# Revit family: PRD_AR_ShwrFttngsPckg_MIRANITShowerPanel_F5LT2024-F5LT2029
name_source: partatom
category: Plumbing Fixtures
units: mm (PartAtom-declared; Revit-internal decimal feet)

## family parameters
Cut with Voids When Loaded = No
Host = Face
OmniClass Number = 23.45.05.14.17
OmniClass Title = Showers
Part Type = Normal
Room Calculation Point = No
Round Connector Dimension = Use Diameter
Shared = No

## types (6) — shared parameters
AccentColour = chrome-look (glossy)
AdditionalConnections = no
AdjustableFlowTime = no
AssetType = Fixed
BasicColour = white
BodyMaterial = PRD_AR_MineralMaterial_Alpinewhite
Category = Pr_40_20_87_75, Shower fittings package
Circulation = no
Color = white
CompatibleA3000Open = no
ConnectionWithPayWaterDispenser = not possible
Default Elevation = 1500 mm  [stored 4.92126 ft]
DiameterNominal = 15  [stored 0.0492126 ft]
DurationUnit = year
FittingMaterial = PRD_AR_ChromatedBrass_HighPolished
FunctionalPrinciple = manual
IfcExportAs = IfcSanitaryTerminalType
IfcExportType = SHOWER
InletSize = G 1/2 A
LockingMechanism = Top section, ceramic
Manufacturer = KWC Group AG
ManufacturerName = KWC Group AG
ManufacturerURL = www.kwc.com
Material = mineral
MaterialCasing = mineral material
MaterialCodeCasing = Miranit
MaterialFitting = brass-look
MinimumFlowPressure = 1 bar
NBSDescription = Shower fittings package
NBSReference = 45-35-70/330
NominalDepth = 100 mm  [stored 0.328084 ft]
NominalHeight = 1160 mm  [stored 3.80577 ft]
NominalLength = 1160 mm  [stored 3.80577 ft]
NominalWidth = 235 mm  [stored 0.770997 ft]
OverallDepth = 100 mm
OverallHeight = 1160 mm
OverallWidth = 235 mm
PositionOfWaterConnection = from top / backside
ProductInformation = http://pim.kwc.com
ProtectiveShutdown = no
ShowerPipeDraining = no
ShowerType = Individual
Size = 235 x 1160 x 100 mm (W x H x D)
SoundInsulation = no
Status = New
SurfaceFinishFitting = chromed
SurfaceTreatmentFitting = polished
TailorMade = no
TemperatureLimit = yes
ThermalDisinfection = yes
TypeOfMixing = with thermostat
TypeOfMounting = wall mounting
TypeOfOperation = manual operation
TypeOfShower = shower panel
URL = www.kwc.com
Uniclass2015Code = Pr_40_20_87_75
Uniclass2015Title = Shower fittings package
Uniclass2015Version = Products v1.32
Version = 1
VolumeFlowRate = 0.15 l/s at 3 bar
WarrantyDurationUnit = year
WaterConnection = hose (gland nut)
WithBackflowPreventer = yes
WithFilter = yes
WithRosettesOrCoverPlate = yes
zero-valued in all types: DrainSize

## per-type parameters (varying)
| type | BIMObjectName | DefaultAutomaticHygieneFlush | Description | Features | ForHandShower | HandShowerVisibility | HasTray | HygieneFlushing | ModelNumber | Name | Parameterization | PositionOfPowerConnection | PowerSupplyConnection | ShowerGelShelf | ShowerHead | ShowerHeadVisibility | TypeOfPowerSupply | TypeOfSensor | WithShowerSet | WithSoapDish | WithTransformerOrPowerSupply |
| F5LT2024 | PRD_AR_ShowerFittingsPackage_MIRANITShowerPanel_F5LT2024 | fixed interval 24 hours | F5L-Therm shower panel made from mineral material for wall mounting with single-lever thermostat DN 15 and connecting nozzle for shower head. For connection to hot and cold water. Function block with integrated mixing cartridge and pre-assembled hygiene unit including sensor with control electronics to perform automatic water hygiene flushing, program-controlled thermal disinfection (additional bypass solenoid-operated flush valve cartridge necessary) and storage of statistical data. Thermostatically-controlled mixer cartridge with expansion element and active scald protection as well as adjustable and turn-proof temperature stop, and ceramic disc technology. All-metal construction, visible parts high-polished, chrome-plated. Connecting nozzles for separate required DN 15 KWC shower head with pre-fitted flow regulator 9.0l/min. Housing with raised function surface made of MIRANIT resin-bonded mineral material with pore-free smooth surface (temperature-resistant up to 80 °C), Alpine white colour. With adjustable and lockable connections with backflow preventer and strainers. Activated hygiene flushing, fixed interval of 24 hours. With option for parameterization and communication via optional, bidirectional remote control. Optional hygiene unit for battery operation with 6 V lithium battery (CR-P2) per fitting or separate power supply via plug-in power supply unit 6.75 V/12 V DC. | For connection to hot and cold water. Housing dimensions 235 x 1160 x 100 mm (W x H x D). Shower head and battery compartment including battery or powersupply unit with extension cable must be ordered separately. | no | No | No | yes | 2030066543 | F5L-Therm MIRANIT shower panel F5LT2024 | remote control | from top / backside | 6.75 / 12 V DC | No | for separately shower head | Yes | Other | opto-electronic sensor | no | no | no |
| F5LT2025 | PRD_AR_ShowerFittingsPackage_MIRANITShowerPanel_F5LT2025 | fixed interval 24 hours | F5L-Therm shower panel made from mineral material for wall mounting with single-lever thermostat DN 15 and hand shower fitting kit. For connection to hot and cold water. Function block with integrated mixing cartridge and pre-assembled hygiene unit including sensor with control electronics to perform automatic water hygiene flushing, program-controlled thermal disinfection (additional bypass solenoid-operated flush valve cartridge necessary) and storage of statistical data. Thermostatically-controlled mixer cartridge with expansion element and active scaldprotection as well as adjustable and turn-proof temperature stop, and ceramic disc technology. All-metal construction, visible parts high-polished, chrome-plated. Pre-fitted chrome-plated brass shower rail with height-adjustable hand shower holder and chrome-plated plastic hand shower, shower head with rain jet, diameter 110 mm, shower hose 900 mm. Housing with raised function surface made of MIRANIT resin-bonded mineral material with pore-free smooth surface (temperature-resistant up to 80 °C), Alpinewhite colour. With adjustable and lockable connections with backflow preventer and strainers. Activated hygiene flushing, fixed interval of 24 hours. With option for parameterization and communication via optional, bidirectional remote control. Optional hygiene unit for battery operation with 6 V lithium battery (CR-P2) per fitting or separate power supply via plug-in power supply unit 6.75 V/12 V DC. | For connection to hot and cold water. Housing dimensions 235 x 1160 x 100 mm (W x H x D). Battery compartment including battery or power supply unit with extension cable must be ordered separately. | yes | Yes | No | yes | 2030066544 | F5L-Therm MIRANIT shower panel with hand shower fitting kit F5LT2025 | remote control |  | 6.75 / 12 V DC | No |  | No | Other | opto-electronic sensor | yes | no | no |
| F5LT2026 | PRD_AR_ShowerFittingsPackage_MIRANITShowerPanel_F5LT2026 | fixed interval 24 hours | F5L-Therm shower panel made from mineral material for wall mounting with single-lever thermostat DN 15 and connecting nozzle for shower head. For connection to hot and cold water. Function block with integrated mixing cartridge and pre-assembled hygiene unit including sensor with control electronics to perform automatic water hygiene flushing, program-controlled thermal disinfection (additional bypass solenoid-operated flush valve cartridge necessary) and storage of statistical data. Thermostatically-controlled mixer cartridge with expansion element and active scald protection as well as adjustable and turn-proof temperature stop, and ceramic disc technology. All-metal construction, visible parts high-polished, chrome-plated. Connecting nozzles for separate required DN 15 KWC shower head with pre-fitted flow regulator 9.0l/min. Housing with raised function surface and seamless moulded shower gel shelf made of MIRANIT resin-bonded mineral material with pore-free smooth surface (temperature-resistant up to 80 °C), Alpine white colour. With adjustable and lockable connections with backflow preventer and strainers. Activated hygiene flushing, fixed interval of 24 hours. With option for parameterization and communication via optional, bidirectional remote control. Optional hygiene unit for battery operation with 6 V lithium battery (CR-P2) per fitting or separate power supply via plug-in power supply unit 6.75 V/12 V DC. | For connection to hot and cold water. Housing dimensions 235 x 1160 x 100 mm (W x H x D). Shower head and battery compartment including battery or power supply unit with extension cable must be ordered separately. | no | No | Yes | yes | 2030066546 | F5L-Therm MIRANIT shower panel with shower gel shelf F5LT2026 | remote control | from top / backside | 6.75 / 12 V DC | Yes | for separately shower head | Yes | Other | opto-electronic sensor | no | integrated | no |
| F5LT2027 | PRD_AR_ShowerFittingsPackage_MIRANITShowerPanel_F5LT2027 |  | F5L-Therm shower panel made from mineral material for wall mounting with single-lever thermostat DN 15 and connecting nozzle for shower head. For connection to hot and cold water. Function block with integrated mixing cartridge and mechanism for an optional water hygiene unit for automatic water hygiene flushing, program-controlled thermal disinfection (additional bypass solenoid-operated flush valve cartridge necessary) and storage of statistical data. Thermostatically-controlled mixer cartridge with expansion element and active scald protection as well as adjustable and turn-proof temperature stop, and ceramic disc technology. All-metal construction, visible parts high-polished, chrome-plated. Connecting nozzles for separate required DN 15 KWC shower head with pre-fitted flow regulator 9.0 l/min. Housing with raised function surface made of MIRANIT resin-bonded mineral material with pore-free smooth surface (temperature-resistant up to 80 °C), Alpine white colour. With adjustable and lockable connections with backflow preventer and strainers. | For connection to hot and cold water. Housing dimensions 235 x 1160 x 100 mm (W x H x D). Shower head must be ordered separately. | no | No | No | prepared | 2030066547 | F5L-Therm MIRANIT shower panel F5LT2027 |  |  |  | No | for separately shower head | Yes |  |  | no | no |  |
| F5LT2028 | PRD_AR_ShowerFittingsPackage_MIRANITShowerPanel_F5LT2028 |  | F5L-Therm shower panel made from mineral material for wall mounting with single-lever thermostat DN 15 and hand shower fitting kit. For connection to hot and cold water. Function block with integrated mixing cartridge and mechanism for an optional water hygiene unit for automatic water hygiene flushing, program-controlled thermal disinfection (additional bypass solenoid-operated flush valve cartridge necessary) and storage of statistical data. Thermostatically-controlled mixer cartridge with expansion element and active scald protection as well as adjustable and turn-proof temperature stop, and ceramic disc technology. All-metal construction, visible parts high-polished, chrome-plated. Pre-fitted chrome-plated brass shower rail with height-adjustable hand shower holder and chrome-plated plastic hand shower, shower head with rain jet, diameter 110 mm, shower hose 900 mm. Housing with raised function surface made of MIRANIT resin-bonded mineral material with pore-free smooth surface (temperature-resistant up to 80 °C), Alpine white colour. With adjustable and lockable connections with backflow preventer and strainers. | For connection to hot and cold water. Housing dimensions 235 x 1160 x 100 mm (W x H x D). | yes | Yes | No | prepared | 2030066548 | F5L-Therm MIRANIT shower panel with hand shower fitting kit F5LT2028 |  |  |  | No |  | No |  |  | yes | no |  |
| F5LT2029 | PRD_AR_ShowerFittingsPackage_MIRANITShowerPanel_F5LT2029 |  | F5L-Therm shower panel made from mineral material for wall mounting with single-lever thermostat DN 15 and connecting nozzle for shower head. For connection to hot and cold water. Function block with integrated mixing cartridge and mechanism for an optional water hygiene unit for automatic water hygiene flushing, program-controlled thermal disinfection (additional bypass solenoid-operated flush valve cartridge necessary) and storage of statistical data. Thermostatically-controlled mixer cartridge with expansion element and active scald protection as well as adjustable and turn-proof temperature stop, and ceramic disc technology. All-metal construction, visible parts high-polished, chrome-plated. Connecting nozzles for separate required DN 15 KWC shower head with pre-fitted flow regulator 9.0 l/min. Housing with raised function surface and seamless moulded shower gel shelf made of MIRANIT resin-bonded mineral material with pore-free smooth surface (temperature-resistant up to 80 °C), Alpine white colour. With adjustable and lockable connections with backflow preventer and strainers. | For connection to hot and cold water. Housing dimensions 235 x 1160 x 100 mm (W x H x D). Shower head must be ordered separately. | no | No | Yes | prepared | 2030066549 | F5L-Therm MIRANIT shower panel with shower gel shelf F5LT2029 |  |  |  | Yes | for separately shower head | Yes |  |  | no | integrated |  |

note: column(s) folded — value = type name in every type: Model, ModelReference

note: [stored X ft] marks values corroborated as IEEE doubles in the binary element streams (Revit-internal decimal feet)

## geometry (parser evidence)
native form markers: Extrusion x1, Sweep x4
no freeform markers — native parametric forms only
